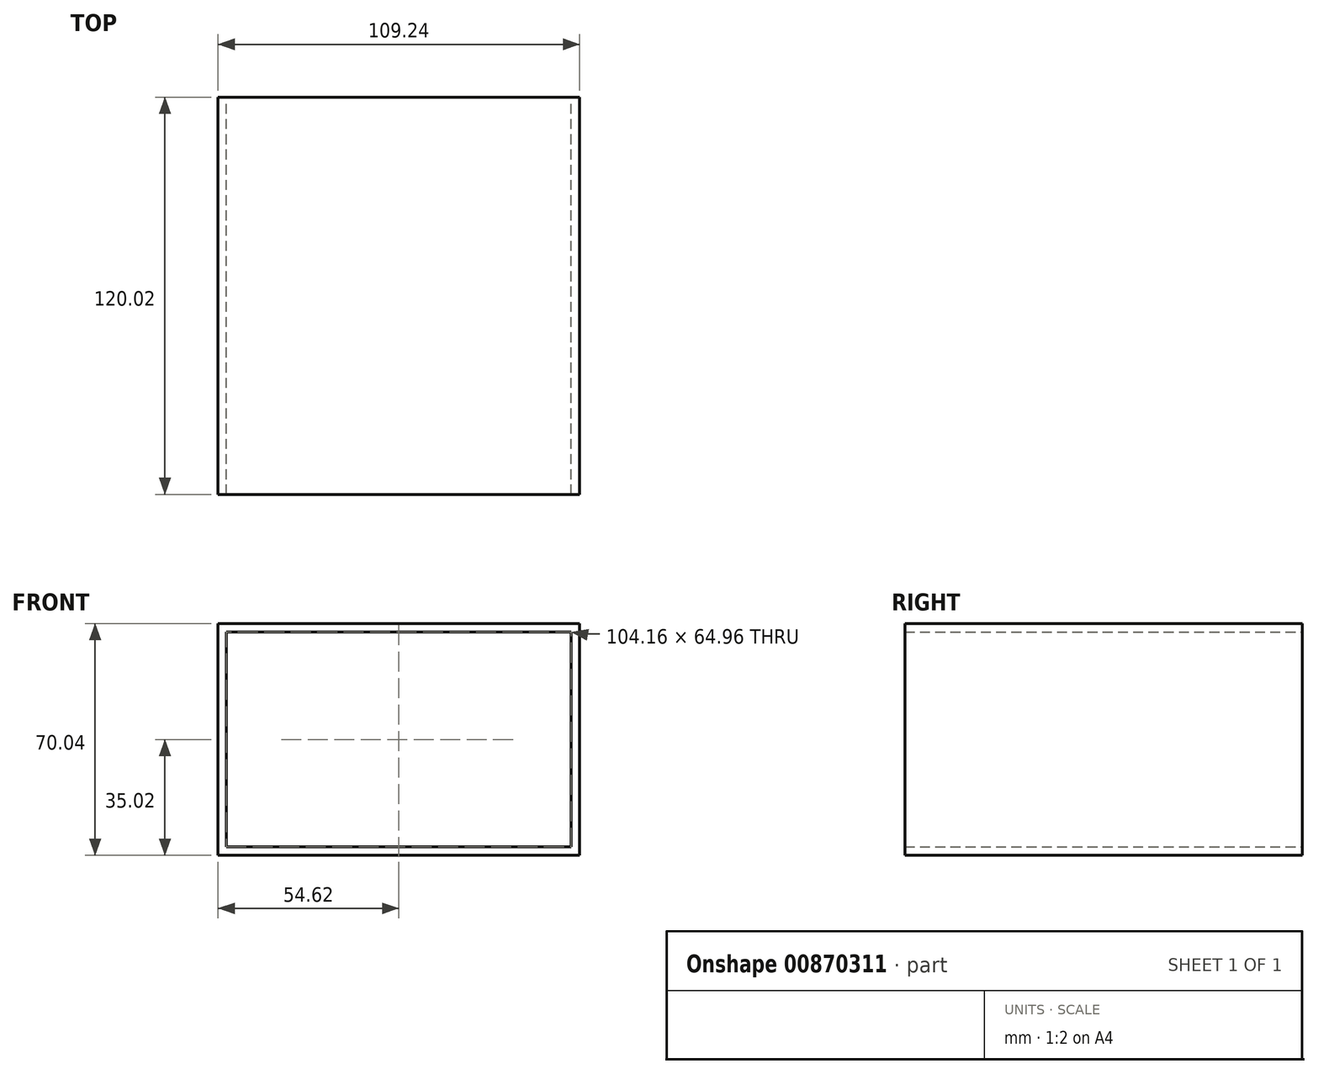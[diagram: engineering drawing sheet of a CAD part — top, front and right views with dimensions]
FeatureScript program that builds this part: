
annotation { "Feature Type Name" : "Feature", "Feature Type Description" : "" }
export const myFeature = defineFeature(function(context is Context, id is Id, definition is map)
    precondition{}
    {
        {
            var Q0;
            Q0=qCreatedBy(makeId("Front.planeOp"),FACE);
            var sketch = newSketch(context, id + "F0", { "sketchPlane" : qUnion([Q0])});
            skLineSegment(sketch, "E0.bottom", {"start": v(-54.62, 35.02) * mm, "end": v(54.62, 35.02) * mm});
            skLineSegment(sketch, "E0.top", {"start": v(-54.62, -35.02) * mm, "end": v(54.62, -35.02) * mm});
            skLineSegment(sketch, "E0.left", {"start": v(-54.62, 35.02) * mm, "end": v(-54.62, -35.02) * mm});
            skLineSegment(sketch, "E0.right", {"start": v(54.62, 35.02) * mm, "end": v(54.62, -35.02) * mm});
            skPoint(sketch, "E0.middle", {"position": v(0, 0) * mm});
            skSolve(sketch);
        }
        {
            var Q0;
            Q0 = qSketchRegion(id + "F0", true);
            var Q1;
            Q1=sQuery(id+"F0.wireOp",EDGE,"E0.left");
            var Q2;
            Q2 = qBodyType(qCreatedBy(id + "F0" ,EDGE), BodyType.WIRE);
            extrude(context, id + "F1", {"entities" : qUnion([Q0]), "surfaceEntities" : qUnion([Q1, Q2]), "endBound" : BoundingType.SYMMETRIC, "depth" : 120.02 * mm, "offsetDistance" : 25.4 * mm});
        }
        {
            var Q0;
            Q0=makeQuery(id+"F1.opExtrude","CAP_FACE",FACE,{"disambiguationData":[OSD([sQuery(id+"F0.wireOp",EDGE,"E0.bottom"),sQuery(id+"F0.wireOp",EDGE,"E0.top"),sQuery(id+"F0.wireOp",EDGE,"E0.left"),sQuery(id+"F0.wireOp",EDGE,"E0.right")])],"isStart":false});
            var Q1;
            Q1=makeQuery(id+"F1.opExtrude","CAP_FACE",FACE,{"disambiguationData":[OSD([sQuery(id+"F0.wireOp",EDGE,"E0.bottom"),sQuery(id+"F0.wireOp",EDGE,"E0.top"),sQuery(id+"F0.wireOp",EDGE,"E0.left"),sQuery(id+"F0.wireOp",EDGE,"E0.right")])],"isStart":true});
            shell(context, id + "F2", {"entities" : qUnion([Q0, Q1]), "thickness" : 2.54 * mm});
        }
    });
